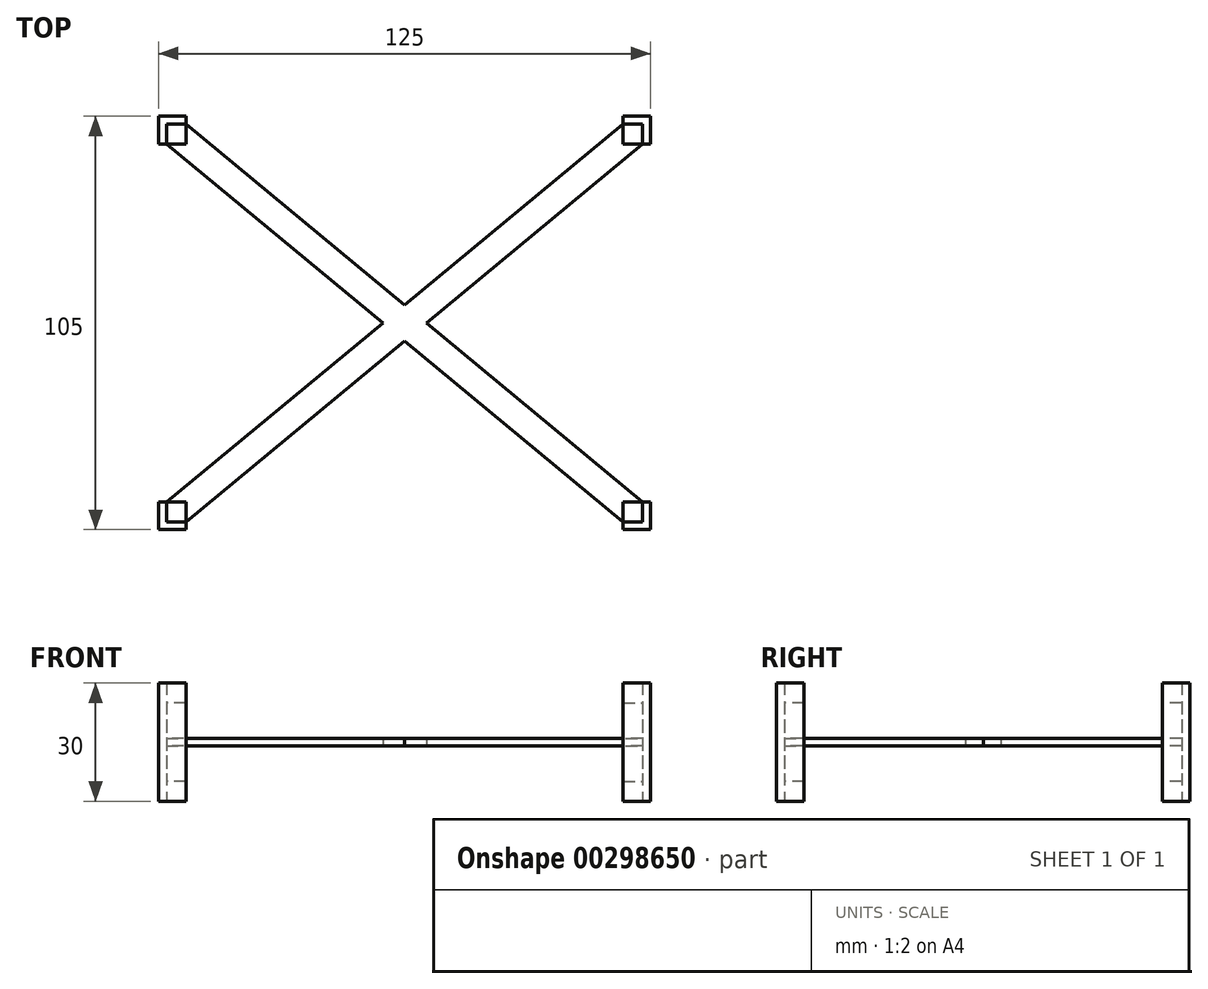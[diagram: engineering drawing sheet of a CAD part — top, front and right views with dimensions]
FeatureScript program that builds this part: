
annotation { "Feature Type Name" : "Feature", "Feature Type Description" : "" }
export const myFeature = defineFeature(function(context is Context, id is Id, definition is map)
    precondition{}
    {
        {
            var Q0;
            Q0=qCreatedBy(makeId("Top.planeOp"),FACE);
            var sketch = newSketch(context, id + "F0", { "sketchPlane" : qUnion([Q0])});
            skLineSegment(sketch, "E0", {"start": v(-70.47, -48.07) * mm, "end": v(-70.47, -55.07) * mm});
            skLineSegment(sketch, "E1", {"start": v(-70.47, -55.07) * mm, "end": v(-63.47, -55.07) * mm});
            skLineSegment(sketch, "E2", {"start": v(-63.47, -55.07) * mm, "end": v(-63.47, -53.07) * mm});
            skLineSegment(sketch, "E3", {"start": v(-63.47, -53.07) * mm, "end": v(-68.47, -53.07) * mm});
            skLineSegment(sketch, "E4", {"start": v(-68.47, -53.07) * mm, "end": v(-68.47, -48.07) * mm});
            skLineSegment(sketch, "E5", {"start": v(-68.47, -48.07) * mm, "end": v(-70.47, -48.07) * mm});
            skLineSegment(sketch, "E6", {"start": v(-63.47, 49.93) * mm, "end": v(-70.47, 49.93) * mm});
            skLineSegment(sketch, "E7", {"start": v(-70.47, 49.93) * mm, "end": v(-70.47, 42.93) * mm});
            skLineSegment(sketch, "E8", {"start": v(-70.47, 42.93) * mm, "end": v(-68.47, 42.93) * mm});
            skLineSegment(sketch, "E9", {"start": v(-68.47, 42.93) * mm, "end": v(-68.47, 47.93) * mm});
            skLineSegment(sketch, "E10", {"start": v(-68.47, 47.93) * mm, "end": v(-63.47, 47.93) * mm});
            skLineSegment(sketch, "E11", {"start": v(-63.47, 47.93) * mm, "end": v(-63.47, 49.93) * mm});
            skLineSegment(sketch, "E12", {"start": v(-68.47, 47.93) * mm, "end": v(-68.47, -53.07) * mm, "construction": true});
            skLineSegment(sketch, "E13", {"start": v(54.53, 42.93) * mm, "end": v(54.53, 49.93) * mm});
            skLineSegment(sketch, "E14", {"start": v(54.53, 49.93) * mm, "end": v(47.53, 49.93) * mm});
            skLineSegment(sketch, "E15", {"start": v(47.53, 49.93) * mm, "end": v(47.53, 47.93) * mm});
            skLineSegment(sketch, "E16", {"start": v(47.53, 47.93) * mm, "end": v(52.53, 47.93) * mm});
            skLineSegment(sketch, "E17", {"start": v(52.53, 47.93) * mm, "end": v(52.53, 42.93) * mm});
            skLineSegment(sketch, "E18", {"start": v(52.53, 42.93) * mm, "end": v(54.53, 42.93) * mm});
            skLineSegment(sketch, "E19", {"start": v(-68.47, 47.93) * mm, "end": v(52.53, 47.93) * mm, "construction": true});
            skLineSegment(sketch, "E20", {"start": v(47.53, -55.07) * mm, "end": v(54.53, -55.07) * mm});
            skLineSegment(sketch, "E21", {"start": v(54.53, -55.07) * mm, "end": v(54.53, -48.07) * mm});
            skLineSegment(sketch, "E22", {"start": v(54.53, -48.07) * mm, "end": v(52.53, -48.07) * mm});
            skLineSegment(sketch, "E23", {"start": v(52.53, -48.07) * mm, "end": v(52.53, -53.07) * mm});
            skLineSegment(sketch, "E24", {"start": v(52.53, -53.07) * mm, "end": v(47.53, -53.07) * mm});
            skLineSegment(sketch, "E25", {"start": v(47.53, -53.07) * mm, "end": v(47.53, -55.07) * mm});
            skLineSegment(sketch, "E26", {"start": v(52.53, 47.93) * mm, "end": v(52.53, -53.07) * mm, "construction": true});
            skLineSegment(sketch, "E27", {"start": v(52.53, -53.07) * mm, "end": v(-68.47, -53.07) * mm, "construction": true});
            skSolve(sketch);
        }
        {
            var Q0;
            Q0 = qSketchRegion(id + "F0", true);
            extrude(context, id + "F1", {"entities" : qUnion([Q0]), "depth" : 30 * mm});
        }
        {
            var Q0;
            Q0=qCreatedBy(makeId("Top.planeOp"),FACE);
            var sketch = newSketch(context, id + "F2", { "sketchPlane" : qUnion([Q0])});
            skLineSegment(sketch, "E28.0", {"start": v(47.53, 47.93) * mm, "end": v(52.53, 47.93) * mm});
            skLineSegment(sketch, "E28.1", {"start": v(52.53, 47.93) * mm, "end": v(52.53, 42.93) * mm});
            skLineSegment(sketch, "E28.2", {"start": v(52.53, -48.07) * mm, "end": v(52.53, -53.07) * mm});
            skLineSegment(sketch, "E28.3", {"start": v(52.53, -53.07) * mm, "end": v(47.53, -53.07) * mm});
            skLineSegment(sketch, "E28.4", {"start": v(-63.47, -53.07) * mm, "end": v(-68.47, -53.07) * mm});
            skLineSegment(sketch, "E28.5", {"start": v(-68.47, -53.07) * mm, "end": v(-68.47, -48.07) * mm});
            skLineSegment(sketch, "E28.6", {"start": v(-68.47, 42.93) * mm, "end": v(-68.47, 47.93) * mm});
            skLineSegment(sketch, "E28.7", {"start": v(-68.47, 47.93) * mm, "end": v(-63.47, 47.93) * mm});
            skLineSegment(sketch, "E29", {"start": v(-68.47, 42.93) * mm, "end": v(-63.47, 42.93) * mm});
            skLineSegment(sketch, "E30", {"start": v(-63.47, 42.93) * mm, "end": v(-63.47, 47.93) * mm});
            skLineSegment(sketch, "E31", {"start": v(52.53, -48.07) * mm, "end": v(47.53, -48.07) * mm});
            skLineSegment(sketch, "E32", {"start": v(47.53, -48.07) * mm, "end": v(47.53, -53.07) * mm});
            skLineSegment(sketch, "E33", {"start": v(-63.47, -53.07) * mm, "end": v(-63.47, -48.07) * mm});
            skLineSegment(sketch, "E34", {"start": v(-63.47, -48.07) * mm, "end": v(-68.47, -48.07) * mm});
            skLineSegment(sketch, "E35", {"start": v(47.53, 47.93) * mm, "end": v(47.53, 42.93) * mm});
            skLineSegment(sketch, "E36", {"start": v(52.53, 42.93) * mm, "end": v(47.53, 42.93) * mm});
            skSolve(sketch);
        }
        {
            var Q0;
            Q0 = qSketchRegion(id + "F2", true);
            extrude(context, id + "F3", {"entities" : qUnion([Q0]), "depth" : 20 * mm});
        }
        {
            var Q0;
            Q0=makeQuery(id+"F3.opExtrude","SWEPT_BODY",BODY,{"disambiguationData":[OSD([sQuery(id+"F2.wireOp",EDGE,"E28.6"),sQuery(id+"F2.wireOp",EDGE,"E28.7"),sQuery(id+"F2.wireOp",EDGE,"E29"),sQuery(id+"F2.wireOp",EDGE,"E30")])]});
            var Q1;
            Q1=makeQuery(id+"F3.opExtrude","SWEPT_BODY",BODY,{"disambiguationData":[OSD([sQuery(id+"F2.wireOp",EDGE,"E28.4"),sQuery(id+"F2.wireOp",EDGE,"E28.5"),sQuery(id+"F2.wireOp",EDGE,"E33"),sQuery(id+"F2.wireOp",EDGE,"E34")])]});
            var Q2;
            Q2=makeQuery(id+"F3.opExtrude","SWEPT_BODY",BODY,{"disambiguationData":[OSD([sQuery(id+"F2.wireOp",EDGE,"E28.2"),sQuery(id+"F2.wireOp",EDGE,"E28.3"),sQuery(id+"F2.wireOp",EDGE,"E31"),sQuery(id+"F2.wireOp",EDGE,"E32")])]});
            var Q3;
            Q3=makeQuery(id+"F3.opExtrude","SWEPT_BODY",BODY,{"disambiguationData":[OSD([sQuery(id+"F2.wireOp",EDGE,"E28.0"),sQuery(id+"F2.wireOp",EDGE,"E28.1"),sQuery(id+"F2.wireOp",EDGE,"E35"),sQuery(id+"F2.wireOp",EDGE,"E36")])]});
            transform(context, id + "F4", {"entities" : qUnion([Q0, Q1, Q2, Q3]), "transformType" : TransformType.TRANSLATION_3D, "dx" : 0 * mm, "dy" : 0 * mm, "dz" : 5 * mm, "makeCopy" : false});
        }
        {
            var Q0;
            Q0=qCreatedBy(makeId("Top.planeOp"),FACE);
            var sketch = newSketch(context, id + "F5", { "sketchPlane" : qUnion([Q0])});
            skLineSegment(sketch, "E37", {"start": v(-63.47, 47.93) * mm, "end": v(52.53, -48.07) * mm});
            skLineSegment(sketch, "E38", {"start": v(47.53, -53.07) * mm, "end": v(-68.47, 42.93) * mm});
            skLineSegment(sketch, "E39", {"start": v(-68.47, -48.07) * mm, "end": v(47.53, 47.93) * mm});
            skLineSegment(sketch, "E40", {"start": v(52.53, 42.93) * mm, "end": v(-63.47, -53.07) * mm});
            skPoint(sketch, "E41.0", {"position": v(-68.47, 47.93) * mm});
            skPoint(sketch, "E41.1", {"position": v(-68.47, -53.07) * mm});
            skPoint(sketch, "E41.2", {"position": v(52.53, -53.07) * mm});
            skPoint(sketch, "E41.3", {"position": v(52.53, 47.93) * mm});
            skLineSegment(sketch, "E42", {"start": v(-68.47, 47.93) * mm, "end": v(-68.47, 42.93) * mm});
            skLineSegment(sketch, "E43", {"start": v(-68.47, 47.93) * mm, "end": v(-63.47, 47.93) * mm});
            skLineSegment(sketch, "E44", {"start": v(47.53, 47.93) * mm, "end": v(52.53, 47.93) * mm});
            skLineSegment(sketch, "E45", {"start": v(52.53, 47.93) * mm, "end": v(52.53, 42.93) * mm});
            skLineSegment(sketch, "E46", {"start": v(52.53, -48.07) * mm, "end": v(52.53, -53.07) * mm});
            skLineSegment(sketch, "E47", {"start": v(52.53, -53.07) * mm, "end": v(47.53, -53.07) * mm});
            skLineSegment(sketch, "E48", {"start": v(-63.47, -53.07) * mm, "end": v(-68.47, -53.07) * mm});
            skLineSegment(sketch, "E49", {"start": v(-68.47, -53.07) * mm, "end": v(-68.47, -48.07) * mm});
            skSolve(sketch);
        }
        {
            var Q0;
            Q0 = qSketchRegion(id + "F5", true);
            extrude(context, id + "F6", {"entities" : qUnion([Q0]), "depth" : 2 * mm});
        }
        {
            var Q0;
            Q0=makeQuery(id+"F6.opExtrude","SWEPT_BODY",BODY,{"disambiguationData":[OSD([sQuery(id+"F5.wireOp",EDGE,"E37"),sQuery(id+"F5.wireOp",EDGE,"E38"),sQuery(id+"F5.wireOp",EDGE,"E39"),sQuery(id+"F5.wireOp",EDGE,"E40"),sQuery(id+"F5.wireOp",EDGE,"E42"),sQuery(id+"F5.wireOp",EDGE,"E43"),sQuery(id+"F5.wireOp",EDGE,"E44"),sQuery(id+"F5.wireOp",EDGE,"E45"),sQuery(id+"F5.wireOp",EDGE,"E46"),sQuery(id+"F5.wireOp",EDGE,"E47"),sQuery(id+"F5.wireOp",EDGE,"E48"),sQuery(id+"F5.wireOp",EDGE,"E49")])]});
            transform(context, id + "F7", {"entities" : qUnion([Q0]), "transformType" : TransformType.TRANSLATION_3D, "dx" : 0 * mm, "dy" : 0 * mm, "dz" : 14 * mm, "makeCopy" : false});
        }
    });
